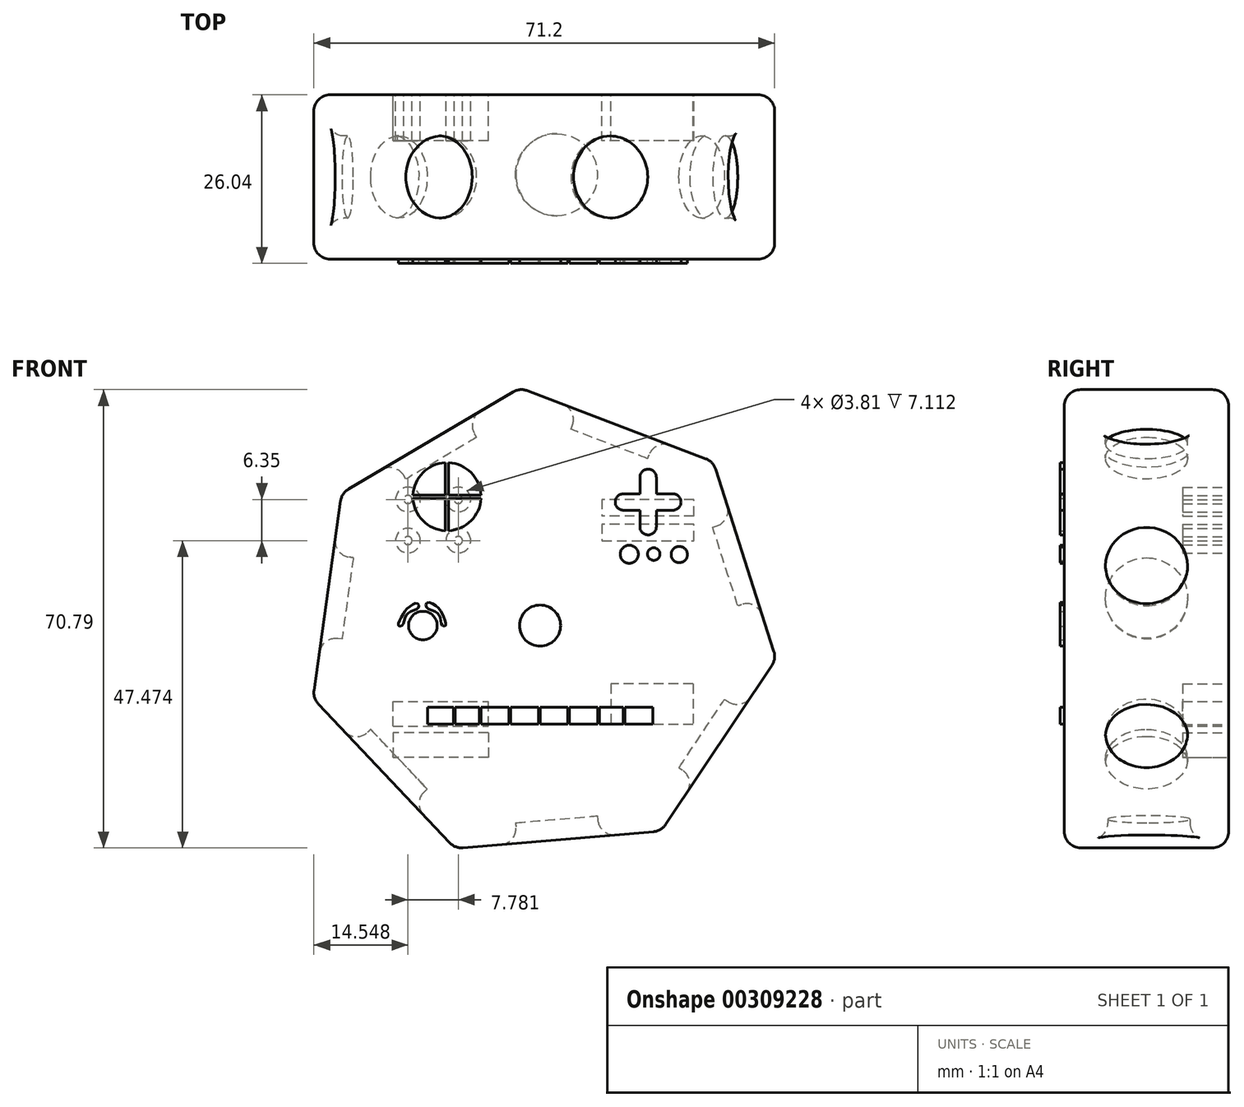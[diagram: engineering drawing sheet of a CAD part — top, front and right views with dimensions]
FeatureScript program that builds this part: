
annotation { "Feature Type Name" : "Feature", "Feature Type Description" : "" }
export const myFeature = defineFeature(function(context is Context, id is Id, definition is map)
    precondition{}
    {
        {
            var Q0;
            Q0=qCreatedBy(makeId("Front.planeOp"),FACE);
            var sketch = newSketch(context, id + "F0", { "sketchPlane" : qUnion([Q0])});
            skCircle(sketch, "E0.cCircle", {"center": v(0, 0) * mm, "radius": 36.85 * mm, "construction": true});
            skLineSegment(sketch, "E0.0", {"start": v(26.77, 25.33) * mm, "end": v(36.49, -5.14) * mm});
            skLineSegment(sketch, "E0.1", {"start": v(36.49, -5.14) * mm, "end": v(18.74, -31.73) * mm});
            skLineSegment(sketch, "E0.2", {"start": v(18.74, -31.73) * mm, "end": v(-13.13, -34.43) * mm});
            skLineSegment(sketch, "E0.3", {"start": v(-13.13, -34.43) * mm, "end": v(-35.1, -11.2) * mm});
            skLineSegment(sketch, "E0.4", {"start": v(-35.1, -11.2) * mm, "end": v(-30.65, 20.46) * mm});
            skLineSegment(sketch, "E0.5", {"start": v(-30.65, 20.46) * mm, "end": v(-3.11, 36.72) * mm});
            skLineSegment(sketch, "E0.6", {"start": v(-3.11, 36.72) * mm, "end": v(26.77, 25.33) * mm});
            skSolve(sketch);
        }
        {
            var Q0;
            Q0 = qSketchRegion(id + "F0", true);
            extrude(context, id + "F1", {"entities" : qUnion([Q0]), "depth" : 25.4 * mm});
        }
        {
            var Q0;
            Q0=makeQuery(id+"F1.opExtrude","SWEPT_FACE",FACE,{"disambiguationData":[OSD([sQuery(id+"F0.wireOp",EDGE,"E0.2")])]});
            var sketch = newSketch(context, id + "F2", { "sketchPlane" : qUnion([Q0])});
            skSolve(sketch);
        }
        {
            var Q0;
            Q0=makeQuery(id+"F1.opExtrude","SWEPT_FACE",FACE,{"disambiguationData":[OSD([sQuery(id+"F0.wireOp",EDGE,"E0.6")])]});
            var sketch = newSketch(context, id + "F3", { "sketchPlane" : qUnion([Q0])});
            skPoint(sketch, "E1", {"position": v(0, -12.7) * mm});
            skCircle(sketch, "E2", {"center": v(0, -12.7) * mm, "radius": 6.35 * mm});
            skSolve(sketch);
        }
        {
            var Q0;
            Q0=makeQuery(id+"F1.opExtrude","SWEPT_FACE",FACE,{"disambiguationData":[OSD([sQuery(id+"F0.wireOp",EDGE,"E0.5")])]});
            var sketch = newSketch(context, id + "F4", { "sketchPlane" : qUnion([Q0])});
            skPoint(sketch, "E3", {"position": v(0, -12.7) * mm});
            skCircle(sketch, "E4", {"center": v(0, -12.7) * mm, "radius": 6.35 * mm});
            skSolve(sketch);
        }
        {
            var Q0;
            Q0=makeQuery(id+"F1.opExtrude","SWEPT_FACE",FACE,{"disambiguationData":[OSD([sQuery(id+"F0.wireOp",EDGE,"E0.0")])]});
            var sketch = newSketch(context, id + "F5", { "sketchPlane" : qUnion([Q0])});
            skPoint(sketch, "E5", {"position": v(-12.7, 0) * mm});
            skCircle(sketch, "E6", {"center": v(-12.7, 0) * mm, "radius": 6.35 * mm});
            skSolve(sketch);
        }
        {
            var Q0;
            Q0=makeQuery(id+"F1.opExtrude","SWEPT_FACE",FACE,{"disambiguationData":[OSD([sQuery(id+"F0.wireOp",EDGE,"E0.1")])]});
            var sketch = newSketch(context, id + "F6", { "sketchPlane" : qUnion([Q0])});
            skCircle(sketch, "E7", {"center": v(-12.7, 0) * mm, "radius": 6.35 * mm});
            skPoint(sketch, "E7.centerSnap0", {"position": v(-12.7, -15.99) * mm});
            skSolve(sketch);
        }
        {
            var Q0;
            {var subQ0=sQuery(id+"F0.wireOp",EDGE,"E0.2");Q0=makeQuery(id+"F2.imprint","IMPRINT",FACE,{"disambiguationData":[TD([[makeQuery(id+"F2.imprint","IMPRINT",EDGE,{"derivedFrom":makeQuery(id+"F1.opExtrude","CAP_EDGE",EDGE,{"disambiguationData":[OSD([subQ0])],"isStart":true})}),-1.0]])]});}
            var sketch = newSketch(context, id + "F7", { "sketchPlane" : qUnion([Q0])});
            skCircle(sketch, "E8", {"center": v(0, 12.35) * mm, "radius": 6.35 * mm});
            skSolve(sketch);
        }
        {
            var Q0;
            Q0=makeQuery(id+"F1.opExtrude","SWEPT_FACE",FACE,{"disambiguationData":[OSD([sQuery(id+"F0.wireOp",EDGE,"E0.3")])]});
            var sketch = newSketch(context, id + "F8", { "sketchPlane" : qUnion([Q0])});
            skCircle(sketch, "E9", {"center": v(12.7, 0) * mm, "radius": 6.35 * mm});
            skPoint(sketch, "E9.centerSnap0", {"position": v(12.7, 15.99) * mm});
            skSolve(sketch);
        }
        {
            var Q0;
            Q0=makeQuery(id+"F1.opExtrude","SWEPT_FACE",FACE,{"disambiguationData":[OSD([sQuery(id+"F0.wireOp",EDGE,"E0.4")])]});
            var sketch = newSketch(context, id + "F9", { "sketchPlane" : qUnion([Q0])});
            skCircle(sketch, "E10", {"center": v(12.7, 0) * mm, "radius": 6.35 * mm});
            skPoint(sketch, "E10.centerSnap0", {"position": v(12.7, 15.99) * mm});
            skPoint(sketch, "E10.centerSnap1", {"position": v(0, 0) * mm});
            skSolve(sketch);
        }
        {
            var Q0;
            Q0 = qSketchRegion(id + "F9", true);
            extrude(context, id + "F10", {"entities" : qUnion([Q0]), "operationType" : NewBodyOperationType.REMOVE, "oppositeDirection" : true, "depth" : 3.17 * mm});
        }
        {
            var Q0;
            Q0=makeQuery(id+"F4.imprint","IMPRINT",FACE,{"disambiguationData":[TD([[makeQuery(id+"F4.imprint","IMPRINT",EDGE,{"derivedFrom":sQuery(id+"F4.wireOp",EDGE,"E4")}),1.0]])]});
            extrude(context, id + "F11", {"entities" : qUnion([Q0]), "operationType" : NewBodyOperationType.REMOVE, "oppositeDirection" : true, "depth" : 3.17 * mm});
        }
        {
            var Q0;
            Q0=makeQuery(id+"F3.imprint","IMPRINT",FACE,{"disambiguationData":[TD([[makeQuery(id+"F3.imprint","IMPRINT",EDGE,{"derivedFrom":sQuery(id+"F3.wireOp",EDGE,"E2")}),1.0]])]});
            extrude(context, id + "F12", {"entities" : qUnion([Q0]), "operationType" : NewBodyOperationType.REMOVE, "oppositeDirection" : true, "depth" : 3.17 * mm});
        }
        {
            var Q0;
            Q0=makeQuery(id+"F5.imprint","IMPRINT",FACE,{"disambiguationData":[TD([[makeQuery(id+"F5.imprint","IMPRINT",EDGE,{"derivedFrom":sQuery(id+"F5.wireOp",EDGE,"E6")}),1.0]])]});
            extrude(context, id + "F13", {"entities" : qUnion([Q0]), "operationType" : NewBodyOperationType.REMOVE, "oppositeDirection" : true, "depth" : 3.17 * mm});
        }
        {
            var Q0;
            Q0=makeQuery(id+"F6.imprint","IMPRINT",FACE,{"disambiguationData":[TD([[makeQuery(id+"F6.imprint","IMPRINT",EDGE,{"derivedFrom":sQuery(id+"F6.wireOp",EDGE,"E7")}),1.0]])]});
            extrude(context, id + "F14", {"entities" : qUnion([Q0]), "operationType" : NewBodyOperationType.REMOVE, "oppositeDirection" : true, "depth" : 3.17 * mm});
        }
        {
            var Q0;
            Q0=makeQuery(id+"F7.imprint","IMPRINT",FACE,{"disambiguationData":[TD([[makeQuery(id+"F7.imprint","IMPRINT",EDGE,{"derivedFrom":sQuery(id+"F7.wireOp",EDGE,"E8")}),1.0]])]});
            extrude(context, id + "F15", {"entities" : qUnion([Q0]), "operationType" : NewBodyOperationType.REMOVE, "oppositeDirection" : true, "depth" : 3.17 * mm});
        }
        {
            var Q0;
            Q0=makeQuery(id+"F8.imprint","IMPRINT",FACE,{"disambiguationData":[TD([[makeQuery(id+"F8.imprint","IMPRINT",EDGE,{"derivedFrom":sQuery(id+"F8.wireOp",EDGE,"E9")}),1.0]])]});
            extrude(context, id + "F16", {"entities" : qUnion([Q0]), "operationType" : NewBodyOperationType.REMOVE, "oppositeDirection" : true, "depth" : 3.17 * mm});
        }
        {
            var Q0;
            Q0=makeQuery(id+"F1.opExtrude","CAP_FACE",FACE,{"disambiguationData":[OSD([sQuery(id+"F0.wireOp",EDGE,"E0.0"),sQuery(id+"F0.wireOp",EDGE,"E0.1"),sQuery(id+"F0.wireOp",EDGE,"E0.2"),sQuery(id+"F0.wireOp",EDGE,"E0.3"),sQuery(id+"F0.wireOp",EDGE,"E0.4"),sQuery(id+"F0.wireOp",EDGE,"E0.5"),sQuery(id+"F0.wireOp",EDGE,"E0.6")])],"isStart":false});
            var sketch = newSketch(context, id + "F17", { "sketchPlane" : qUnion([Q0])});
            skCircle(sketch, "E11", {"center": v(0, 0) * mm, "radius": 3.18 * mm});
            skLineSegment(sketch, "E12", {"start": v(15.42, 22.9) * mm, "end": v(15.42, 20.35) * mm});
            skLineSegment(sketch, "E13", {"start": v(15.42, 20.35) * mm, "end": v(12.88, 20.35) * mm});
            skLineSegment(sketch, "E14", {"start": v(12.88, 17.81) * mm, "end": v(15.42, 17.81) * mm});
            skLineSegment(sketch, "E15", {"start": v(15.42, 17.81) * mm, "end": v(15.42, 15.27) * mm});
            skLineSegment(sketch, "E16", {"start": v(17.96, 15.27) * mm, "end": v(17.96, 17.81) * mm});
            skLineSegment(sketch, "E17", {"start": v(17.96, 17.81) * mm, "end": v(20.5, 17.81) * mm});
            skLineSegment(sketch, "E18", {"start": v(20.5, 20.35) * mm, "end": v(17.96, 20.35) * mm});
            skLineSegment(sketch, "E19", {"start": v(17.96, 20.35) * mm, "end": v(17.96, 22.9) * mm});
            skArc(sketch, "E20", {"start": v(17.96, 22.9) * mm, "mid": v(16.7, 24.16) * mm, "end": v(15.42, 22.9) * mm});
            skArc(sketch, "E21", {"start": v(20.5, 17.81) * mm, "mid": v(21.77, 19.08) * mm, "end": v(20.5, 20.35) * mm});
            skArc(sketch, "E22", {"start": v(15.42, 15.27) * mm, "mid": v(16.7, 14) * mm, "end": v(17.96, 15.27) * mm});
            skArc(sketch, "E23", {"start": v(12.88, 20.35) * mm, "mid": v(11.61, 19.08) * mm, "end": v(12.88, 17.81) * mm});
            skCircle(sketch, "E24", {"center": v(21.5, 10.97) * mm, "radius": 1.26 * mm});
            skCircle(sketch, "E25", {"center": v(17.55, 11.04) * mm, "radius": 0.97 * mm});
            skCircle(sketch, "E26", {"center": v(13.78, 11.02) * mm, "radius": 1.4 * mm});
            skCircle(sketch, "E27", {"center": v(-18.1, 0) * mm, "radius": 2.21 * mm});
            skFitSpline(sketch, "E28", {"points": [v(-21.33, 0) * mm, v(-20.9, 1.12) * mm, v(-19.96, 2.2) * mm, v(-18.76, 2.83) * mm, v(-18.96, 3.43) * mm, v(-20.27, 2.86) * mm, v(-21.39, 1.37) * mm, v(-21.87, 0) * mm, v(-21.33, 0) * mm]});
            skFitSpline(sketch, "E29", {"points": [v(-15.08, 0) * mm, v(-15.42, 1.14) * mm, v(-16.08, 2.09) * mm, v(-17.59, 2.89) * mm, v(-17.42, 3.54) * mm, v(-15.76, 2.77) * mm, v(-14.88, 1.23) * mm, v(-14.6, 0) * mm, v(-15.08, 0) * mm]});
            skCircle(sketch, "E30", {"center": v(-14.38, 19.91) * mm, "radius": 5.26 * mm});
            skLineSegment(sketch, "E31", {"start": v(-14.13, 25.17) * mm, "end": v(-14.13, 19.91) * mm});
            skLineSegment(sketch, "E32", {"start": v(-14.63, 25.17) * mm, "end": v(-14.63, 19.91) * mm});
            skLineSegment(sketch, "E33", {"start": v(-14.13, 19.91) * mm, "end": v(-14.13, 14.66) * mm});
            skLineSegment(sketch, "E34", {"start": v(-14.63, 19.91) * mm, "end": v(-14.63, 14.66) * mm});
            skLineSegment(sketch, "E35", {"start": v(-9.12, 19.66) * mm, "end": v(-14.13, 19.66) * mm});
            skLineSegment(sketch, "E36", {"start": v(-9.12, 20.17) * mm, "end": v(-14.13, 20.17) * mm});
            skLineSegment(sketch, "E37", {"start": v(-14.63, 19.66) * mm, "end": v(-19.64, 19.66) * mm});
            skLineSegment(sketch, "E38", {"start": v(-14.63, 20.17) * mm, "end": v(-19.64, 20.17) * mm});
            skLineSegment(sketch, "E39.bottom", {"start": v(-17.4, -12.62) * mm, "end": v(17.4, -12.62) * mm});
            skLineSegment(sketch, "E39.top", {"start": v(-17.4, -15.22) * mm, "end": v(17.4, -15.22) * mm});
            skLineSegment(sketch, "E39.left", {"start": v(-17.4, -12.62) * mm, "end": v(-17.4, -15.22) * mm});
            skLineSegment(sketch, "E39.right", {"start": v(17.4, -12.62) * mm, "end": v(17.4, -15.22) * mm});
            skLineSegment(sketch, "E40", {"start": v(0, -15.22) * mm, "end": v(0, -12.62) * mm});
            skLineSegment(sketch, "E41", {"start": v(-9.4, -15.22) * mm, "end": v(-9.4, -12.62) * mm});
            skLineSegment(sketch, "E42", {"start": v(9.15, -12.62) * mm, "end": v(9.15, -15.22) * mm});
            skLineSegment(sketch, "E43", {"start": v(-4.83, -12.62) * mm, "end": v(-4.83, -15.22) * mm});
            skLineSegment(sketch, "E44", {"start": v(-13.36, -12.62) * mm, "end": v(-13.36, -15.22) * mm});
            skLineSegment(sketch, "E45", {"start": v(4.25, -12.62) * mm, "end": v(4.25, -15.22) * mm});
            skLineSegment(sketch, "E46", {"start": v(12.86, -12.62) * mm, "end": v(12.86, -15.22) * mm});
            skLineSegment(sketch, "E47", {"start": v(-13.1, -12.62) * mm, "end": v(-13.1, -15.22) * mm});
            skLineSegment(sketch, "E48", {"start": v(-9.15, -12.62) * mm, "end": v(-9.15, -15.22) * mm});
            skLineSegment(sketch, "E49", {"start": v(-4.57, -12.62) * mm, "end": v(-4.57, -15.22) * mm});
            skLineSegment(sketch, "E50", {"start": v(-0.26, -12.62) * mm, "end": v(-0.26, -15.22) * mm});
            skLineSegment(sketch, "E51", {"start": v(4.5, -12.62) * mm, "end": v(4.5, -15.22) * mm});
            skLineSegment(sketch, "E52", {"start": v(8.9, -12.62) * mm, "end": v(8.9, -15.22) * mm});
            skLineSegment(sketch, "E53", {"start": v(13.12, -12.62) * mm, "end": v(13.12, -15.22) * mm});
            skSolve(sketch);
        }
        {
            var Q0;
            Q0=makeQuery(id+"F17.imprint","IMPRINT",FACE,{"disambiguationData":[TD([[makeQuery(id+"F17.imprint","IMPRINT",EDGE,{"derivedFrom":sQuery(id+"F17.wireOp",EDGE,"E11")}),1.0]])]});
            var Q1;
            Q1=makeQuery(id+"F17.imprint","IMPRINT",FACE,{"disambiguationData":[TD([[makeQuery(id+"F17.imprint","IMPRINT",EDGE,{"derivedFrom":sQuery(id+"F17.wireOp",EDGE,"E12")}),1.0]])]});
            var Q2;
            Q2=makeQuery(id+"F17.imprint","IMPRINT",FACE,{"disambiguationData":[TD([[makeQuery(id+"F17.imprint","IMPRINT",EDGE,{"derivedFrom":sQuery(id+"F17.wireOp",EDGE,"E24")}),1.0]])]});
            var Q3;
            Q3=makeQuery(id+"F17.imprint","IMPRINT",FACE,{"disambiguationData":[TD([[makeQuery(id+"F17.imprint","IMPRINT",EDGE,{"derivedFrom":sQuery(id+"F17.wireOp",EDGE,"E25")}),1.0]])]});
            var Q4;
            Q4=makeQuery(id+"F17.imprint","IMPRINT",FACE,{"disambiguationData":[TD([[makeQuery(id+"F17.imprint","IMPRINT",EDGE,{"derivedFrom":sQuery(id+"F17.wireOp",EDGE,"E26")}),1.0]])]});
            var Q5;
            Q5=makeQuery(id+"F17.imprint","IMPRINT",FACE,{"disambiguationData":[TD([[makeQuery(id+"F17.imprint","IMPRINT",EDGE,{"derivedFrom":sQuery(id+"F17.wireOp",EDGE,"E27")}),1.0]])]});
            var Q6;
            Q6=makeQuery(id+"F17.imprint","IMPRINT",FACE,{"disambiguationData":[TD([[makeQuery(id+"F17.imprint","IMPRINT",EDGE,{"derivedFrom":sQuery(id+"F17.wireOp",EDGE,"E28")}),1.0]])]});
            var Q7;
            Q7=makeQuery(id+"F17.imprint","IMPRINT",FACE,{"disambiguationData":[TD([[makeQuery(id+"F17.imprint","IMPRINT",EDGE,{"derivedFrom":sQuery(id+"F17.wireOp",EDGE,"E29")}),-1.0]])]});
            var Q8;
            {var subQ3=sQuery(id+"F17.wireOp",EDGE,"E36");Q8=makeQuery(id+"F17.imprint","IMPRINT",FACE,{"disambiguationData":[TD([[makeQuery(id+"F17.imprint","IMPRINT",EDGE,{"derivedFrom":subQ3}),-1.0]])]});}
            var Q9;
            {var subQ3=sQuery(id+"F17.wireOp",EDGE,"E38");Q9=makeQuery(id+"F17.imprint","IMPRINT",FACE,{"disambiguationData":[TD([[makeQuery(id+"F17.imprint","IMPRINT",EDGE,{"derivedFrom":subQ3}),-1.0]])]});}
            var Q10;
            {var subQ3=sQuery(id+"F17.wireOp",EDGE,"E37");Q10=makeQuery(id+"F17.imprint","IMPRINT",FACE,{"disambiguationData":[TD([[makeQuery(id+"F17.imprint","IMPRINT",EDGE,{"derivedFrom":subQ3}),1.0]])]});}
            var Q11;
            {var subQ3=sQuery(id+"F17.wireOp",EDGE,"E35");Q11=makeQuery(id+"F17.imprint","IMPRINT",FACE,{"disambiguationData":[TD([[makeQuery(id+"F17.imprint","IMPRINT",EDGE,{"derivedFrom":subQ3}),1.0]])]});}
            var Q12;
            {var subQ0=sQuery(id+"F17.wireOp",EDGE,"E43");Q12=makeQuery(id+"F17.imprint","IMPRINT",FACE,{"disambiguationData":[TD([[makeQuery(id+"F17.imprint","IMPRINT",EDGE,{"derivedFrom":subQ0}),-1.0]])]});}
            var Q13;
            {var subQ0=sQuery(id+"F17.wireOp",EDGE,"E41");Q13=makeQuery(id+"F17.imprint","IMPRINT",FACE,{"disambiguationData":[TD([[makeQuery(id+"F17.imprint","IMPRINT",EDGE,{"derivedFrom":subQ0}),1.0]])]});}
            var Q14;
            {var subQ0=sQuery(id+"F17.wireOp",EDGE,"E39.left");Q14=makeQuery(id+"F17.imprint","IMPRINT",FACE,{"disambiguationData":[TD([[makeQuery(id+"F17.imprint","IMPRINT",EDGE,{"derivedFrom":subQ0}),1.0]])]});}
            var Q15;
            {var subQ0=sQuery(id+"F17.wireOp",EDGE,"E49");Q15=makeQuery(id+"F17.imprint","IMPRINT",FACE,{"disambiguationData":[TD([[makeQuery(id+"F17.imprint","IMPRINT",EDGE,{"derivedFrom":subQ0}),1.0]])]});}
            var Q16;
            {var subQ0=sQuery(id+"F17.wireOp",EDGE,"E40");Q16=makeQuery(id+"F17.imprint","IMPRINT",FACE,{"disambiguationData":[TD([[makeQuery(id+"F17.imprint","IMPRINT",EDGE,{"derivedFrom":subQ0}),-1.0]])]});}
            var Q17;
            {var subQ0=sQuery(id+"F17.wireOp",EDGE,"E51");Q17=makeQuery(id+"F17.imprint","IMPRINT",FACE,{"disambiguationData":[TD([[makeQuery(id+"F17.imprint","IMPRINT",EDGE,{"derivedFrom":subQ0}),1.0]])]});}
            var Q18;
            {var subQ0=sQuery(id+"F17.wireOp",EDGE,"E42");Q18=makeQuery(id+"F17.imprint","IMPRINT",FACE,{"disambiguationData":[TD([[makeQuery(id+"F17.imprint","IMPRINT",EDGE,{"derivedFrom":subQ0}),1.0]])]});}
            var Q19;
            {var subQ0=sQuery(id+"F17.wireOp",EDGE,"E39.right");Q19=makeQuery(id+"F17.imprint","IMPRINT",FACE,{"disambiguationData":[TD([[makeQuery(id+"F17.imprint","IMPRINT",EDGE,{"derivedFrom":subQ0}),-1.0]])]});}
            extrude(context, id + "F18", {"entities" : qUnion([Q0, Q1, Q2, Q3, Q4, Q5, Q6, Q7, Q8, Q9, Q10, Q11, Q12, Q13, Q14, Q15, Q16, Q17, Q18, Q19]), "operationType" : NewBodyOperationType.ADD, "depth" : 0.64 * mm});
        }
        {
            var Q0;
            Q0=makeQuery(id+"F1.opExtrude","CAP_FACE",FACE,{"disambiguationData":[OSD([sQuery(id+"F0.wireOp",EDGE,"E0.0"),sQuery(id+"F0.wireOp",EDGE,"E0.1"),sQuery(id+"F0.wireOp",EDGE,"E0.2"),sQuery(id+"F0.wireOp",EDGE,"E0.3"),sQuery(id+"F0.wireOp",EDGE,"E0.4"),sQuery(id+"F0.wireOp",EDGE,"E0.5"),sQuery(id+"F0.wireOp",EDGE,"E0.6")])],"isStart":true});
            var sketch = newSketch(context, id + "F19", { "sketchPlane" : qUnion([Q0])});
            skLineSegment(sketch, "E54", {"start": v(-23.77, 19.48) * mm, "end": v(-9.57, 19.48) * mm});
            skLineSegment(sketch, "E55", {"start": v(-9.57, 19.48) * mm, "end": v(-9.57, 13.13) * mm});
            skLineSegment(sketch, "E56", {"start": v(-9.57, 13.13) * mm, "end": v(-23.77, 13.13) * mm});
            skLineSegment(sketch, "E57", {"start": v(-23.77, 13.13) * mm, "end": v(-23.77, 19.48) * mm});
            skCircle(sketch, "E58", {"center": v(12.63, 19.48) * mm, "radius": 1.9 * mm});
            skCircle(sketch, "E59", {"center": v(20.41, 19.48) * mm, "radius": 1.9 * mm});
            skCircle(sketch, "E60", {"center": v(12.63, 13.13) * mm, "radius": 1.9 * mm});
            skCircle(sketch, "E61", {"center": v(20.41, 13.13) * mm, "radius": 1.9 * mm});
            skLineSegment(sketch, "E62.bottom", {"start": v(-23.64, -9.01) * mm, "end": v(-10.94, -9.01) * mm});
            skLineSegment(sketch, "E62.top", {"start": v(-23.64, -15.27) * mm, "end": v(-10.94, -15.27) * mm});
            skLineSegment(sketch, "E62.left", {"start": v(-23.64, -9.01) * mm, "end": v(-23.64, -15.27) * mm});
            skLineSegment(sketch, "E62.right", {"start": v(-10.94, -9.01) * mm, "end": v(-10.94, -15.27) * mm});
            skLineSegment(sketch, "E63.bottom", {"start": v(8, -16.53) * mm, "end": v(22.69, -16.53) * mm});
            skLineSegment(sketch, "E63.top", {"start": v(8, -20.34) * mm, "end": v(22.69, -20.34) * mm});
            skLineSegment(sketch, "E63.left", {"start": v(8, -16.53) * mm, "end": v(8, -20.34) * mm});
            skLineSegment(sketch, "E63.right", {"start": v(22.69, -16.53) * mm, "end": v(22.69, -20.34) * mm});
            skLineSegment(sketch, "E64.bottom", {"start": v(22.69, -15.54) * mm, "end": v(8, -15.54) * mm});
            skLineSegment(sketch, "E64.top", {"start": v(22.69, -11.73) * mm, "end": v(8, -11.73) * mm});
            skLineSegment(sketch, "E64.left", {"start": v(22.69, -15.54) * mm, "end": v(22.69, -11.73) * mm});
            skLineSegment(sketch, "E64.right", {"start": v(8, -15.54) * mm, "end": v(8, -11.73) * mm});
            skCircle(sketch, "E65", {"center": v(12.63, 13.13) * mm, "radius": 0.64 * mm});
            skCircle(sketch, "E66", {"center": v(12.63, 19.48) * mm, "radius": 0.64 * mm});
            skCircle(sketch, "E67", {"center": v(20.41, 19.48) * mm, "radius": 0.64 * mm});
            skCircle(sketch, "E68", {"center": v(20.41, 13.13) * mm, "radius": 0.64 * mm});
            skLineSegment(sketch, "E69", {"start": v(-23.77, 16.94) * mm, "end": v(-9.57, 16.94) * mm});
            skLineSegment(sketch, "E70", {"start": v(-23.77, 15.67) * mm, "end": v(-9.57, 15.67) * mm});
            skSolve(sketch);
        }
        {
            var Q0;
            Q0=makeQuery(id+"F19.imprint","IMPRINT",FACE,{"disambiguationData":[TD([[makeQuery(id+"F19.imprint","IMPRINT",EDGE,{"derivedFrom":sQuery(id+"F19.wireOp",EDGE,"E62.bottom")}),-1.0]])]});
            var Q1;
            Q1=makeQuery(id+"F19.imprint","IMPRINT",FACE,{"disambiguationData":[TD([[makeQuery(id+"F19.imprint","IMPRINT",EDGE,{"derivedFrom":sQuery(id+"F19.wireOp",EDGE,"E64.bottom")}),-1.0]])]});
            var Q2;
            Q2=makeQuery(id+"F19.imprint","IMPRINT",FACE,{"disambiguationData":[TD([[makeQuery(id+"F19.imprint","IMPRINT",EDGE,{"derivedFrom":sQuery(id+"F19.wireOp",EDGE,"E63.bottom")}),-1.0]])]});
            var Q3;
            Q3=makeQuery(id+"F19.imprint","IMPRINT",FACE,{"disambiguationData":[TD([[makeQuery(id+"F19.imprint","IMPRINT",EDGE,{"derivedFrom":sQuery(id+"F19.wireOp",EDGE,"E60")}),1.0]])]});
            var Q4;
            Q4=makeQuery(id+"F19.imprint","IMPRINT",FACE,{"disambiguationData":[TD([[makeQuery(id+"F19.imprint","IMPRINT",EDGE,{"derivedFrom":sQuery(id+"F19.wireOp",EDGE,"E61")}),1.0]])]});
            var Q5;
            Q5=makeQuery(id+"F19.imprint","IMPRINT",FACE,{"disambiguationData":[TD([[makeQuery(id+"F19.imprint","IMPRINT",EDGE,{"derivedFrom":sQuery(id+"F19.wireOp",EDGE,"E59")}),1.0]])]});
            var Q6;
            Q6=makeQuery(id+"F19.imprint","IMPRINT",FACE,{"disambiguationData":[TD([[makeQuery(id+"F19.imprint","IMPRINT",EDGE,{"derivedFrom":sQuery(id+"F19.wireOp",EDGE,"E58")}),1.0]])]});
            var Q7;
            {var subQ0=sQuery(id+"F19.wireOp",EDGE,"E54");Q7=makeQuery(id+"F19.imprint","IMPRINT",FACE,{"disambiguationData":[TD([[makeQuery(id+"F19.imprint","IMPRINT",EDGE,{"derivedFrom":subQ0}),-1.0]])]});}
            var Q8;
            {var subQ0=sQuery(id+"F19.wireOp",EDGE,"E56");Q8=makeQuery(id+"F19.imprint","IMPRINT",FACE,{"disambiguationData":[TD([[makeQuery(id+"F19.imprint","IMPRINT",EDGE,{"derivedFrom":subQ0}),-1.0]])]});}
            extrude(context, id + "F20", {"entities" : qUnion([Q0, Q1, Q2, Q3, Q4, Q5, Q6, Q7, Q8]), "operationType" : NewBodyOperationType.REMOVE, "oppositeDirection" : true, "depth" : 7.11 * mm});
        }
        {
            var Q0;
            Q0=makeQuery(id+"F1.opExtrude","SWEPT_FACE",FACE,{"disambiguationData":[OSD([sQuery(id+"F0.wireOp",EDGE,"E0.4")])]});
            var Q1;
            Q1=makeQuery(id+"F1.opExtrude","SWEPT_FACE",FACE,{"disambiguationData":[OSD([sQuery(id+"F0.wireOp",EDGE,"E0.5")])]});
            var Q2;
            Q2=makeQuery(id+"F1.opExtrude","SWEPT_FACE",FACE,{"disambiguationData":[OSD([sQuery(id+"F0.wireOp",EDGE,"E0.6")])]});
            var Q3;
            Q3=makeQuery(id+"F1.opExtrude","SWEPT_FACE",FACE,{"disambiguationData":[OSD([sQuery(id+"F0.wireOp",EDGE,"E0.0")])]});
            var Q4;
            Q4=makeQuery(id+"F1.opExtrude","SWEPT_FACE",FACE,{"disambiguationData":[OSD([sQuery(id+"F0.wireOp",EDGE,"E0.1")])]});
            var Q5;
            Q5=makeQuery(id+"F1.opExtrude","SWEPT_FACE",FACE,{"disambiguationData":[OSD([sQuery(id+"F0.wireOp",EDGE,"E0.2")])]});
            var Q6;
            Q6=makeQuery(id+"F1.opExtrude","SWEPT_FACE",FACE,{"disambiguationData":[OSD([sQuery(id+"F0.wireOp",EDGE,"E0.3")])]});
            fillet(context, id + "F21", {"entities" : qUnion([Q0, Q1, Q2, Q3, Q4, Q5, Q6]), "radius" : 2.54 * mm, "tangentPropagation" : true, "allowEdgeOverflow" : false});
        }
    });
